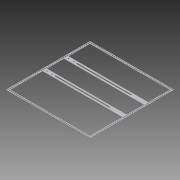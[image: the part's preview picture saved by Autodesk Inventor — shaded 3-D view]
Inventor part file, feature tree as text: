
AUTODESK INVENTOR PART (.ipt)
format: ipt  version: 2013 (Build 170138000, 138)  size: 9,556,480 bytes
history: native  units: in
note: dims shown in document units (in); Inventor stores cm internally (conversion verified against a paired STEP export)
features: reference x4, sketch x3, other x3, sheet_metal_op x2, extrude x1
ambient origin geometry x8: Origin, YZ Plane, XZ Plane, XY Plane, X Axis, Y Axis, Z Axis, Center Point
feature tree (13):
  extrude  "Extrusion2"  Depth=0.5in
  sheet_metal_op  "Face1"
  sketch  "Sketch2"  dims[d0=0.5in d3=0.5in]
  other  "Plate1"
  sheet_metal_op  "Bend1"
  sketch  "Sketch8"  dims[d4=0.5in]
  sketch  "Sketch9"  dims[d6=15.5in d7=14.1732in d9=0.4357in d10=0.3937in d12=1.0in d14=13.7795in d16=0.4357in d17=0.3937in d19=1.0in d21=19.25in d22=19.685in d24=0.3878in d25=0.3937in d27=1.0in d36=15.5in d42=0.4357in d43=0.25in d44=14.1732in d46=0.4357in d47=0.3937in d49=1.0in d51=18.5in d52=9.25in d53=0.125in d54=0.0in d55=1.0in d58=1.0in d59=5.0in d60=4.0in d61=0.125in d62=0.125in d63=0.0625in d64=0.25in d65=0.125in d96=0.266in d97=0.5in d98=3.5in d99=0.266in d100=0.5in d101=3.0in d102=0.266in d103=3.5in d104=0.5in d105=0.266in d106=0.5in d107=3.0in d108=0.125in d109=0.0in d110=0.125in d111=0.0in]
  reference  "Reference4"
  reference  "Reference5"
  reference  "Reference6"
  reference  "Reference7"
  other  "Cut6"
  other  "Cut7"
